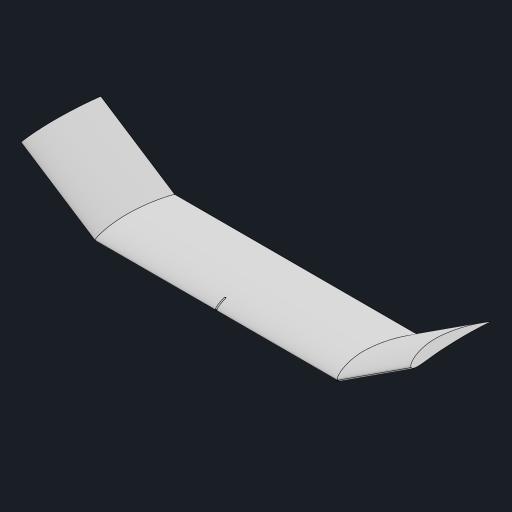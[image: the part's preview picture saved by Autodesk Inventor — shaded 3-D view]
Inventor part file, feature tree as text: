
AUTODESK INVENTOR PART (.ipt)
format: ipt  version: 2023 (Build 270158000, 158)  size: 335,872 bytes
history: native  units: mm
features: sketch x5, extrude x4, other x2, mirror x1
ambient origin geometry x8: Origin, YZ Plane, XZ Plane, XY Plane, X Axis, Y Axis, Z Axis, Center Point
bodies: Body1 (feature_tree)
feature tree (12):
  other  "ソリッド1"
  sketch  "スケッチ1"
  extrude  "押し出し1"  Depth=180.0mm TaperAngle=0.0deg
  extrude  "押し出し2"  Depth=250.0mm TaperAngle=0.0deg
  sketch  "スケッチ5"
  other  "作業平面2"
  extrude  "押し出し3"  [1 undecoded]
  mirror  "ミラー1"
  extrude  "押し出し5"  Depth=180.0mm
  sketch  "スケッチ2"
  sketch  "スケッチ6"
  sketch  "スケッチ8"
note: 1 required parameter value undecoded (feature->parameter linkage not recoverable at this tier; creation-order binding heuristic only, values carry confidence <= 0.55)
